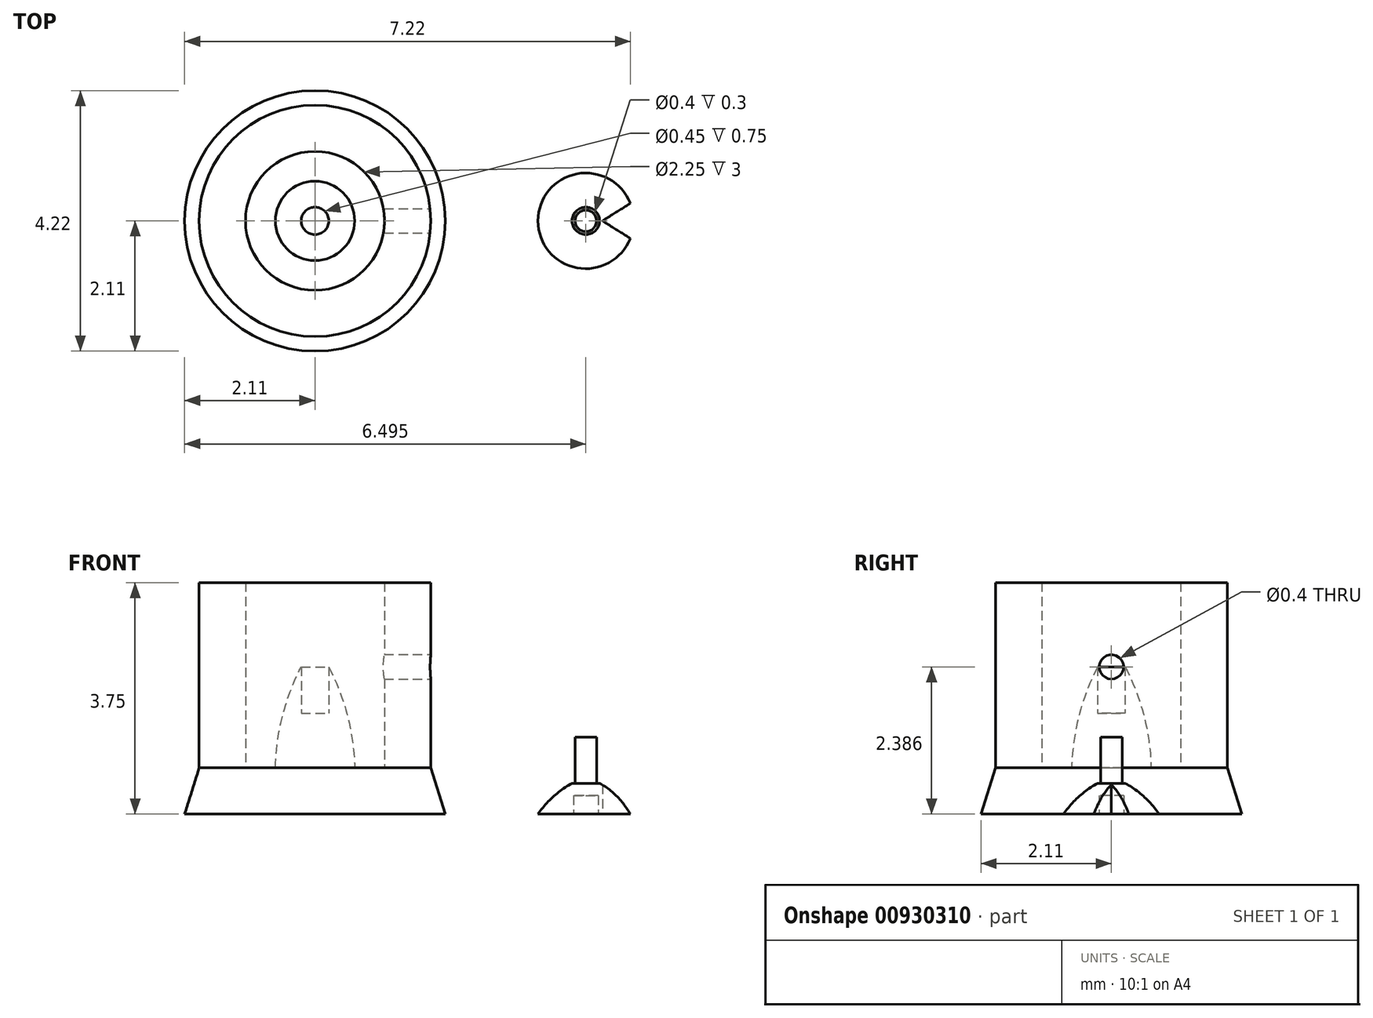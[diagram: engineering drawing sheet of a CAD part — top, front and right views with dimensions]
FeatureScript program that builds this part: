
annotation { "Feature Type Name" : "Feature", "Feature Type Description" : "" }
export const myFeature = defineFeature(function(context is Context, id is Id, definition is map)
    precondition{}
    {
        {
            var Q0;
            Q0=qCreatedBy(makeId("Front.planeOp"),FACE);
            var sketch = newSketch(context, id + "F0", { "sketchPlane" : qUnion([Q0])});
            skLineSegment(sketch, "E0", {"start": v(0, 0) * mm, "end": v(0, 0.89) * mm});
            skLineSegment(sketch, "E1", {"start": v(0.64, 0) * mm, "end": v(0.78, 0) * mm});
            skArc(sketch, "E2", {"start": v(0.78, 0) * mm, "mid": v(0.78, 0.1) * mm, "end": v(0.78, 0.2) * mm});
            skLineSegment(sketch, "E3", {"start": v(0.78, 0) * mm, "end": v(0.78, 25.4) * mm});
            skLineSegment(sketch, "E4", {"start": v(0.22, 1.55) * mm, "end": v(0.22, 1.64) * mm});
            skLineSegment(sketch, "E5", {"start": v(0.22, 1.64) * mm, "end": v(0.22, 0.89) * mm});
            skLineSegment(sketch, "E6", {"start": v(0.22, 0.89) * mm, "end": v(0, 0.89) * mm});
            skLineSegment(sketch, "E7", {"start": v(0.78, 0) * mm, "end": v(1.13, 0) * mm});
            skLineSegment(sketch, "E8", {"start": v(1.13, 0) * mm, "end": v(1.13, 3) * mm});
            skLineSegment(sketch, "E9", {"start": v(1.13, 3) * mm, "end": v(1.88, 3) * mm});
            skLineSegment(sketch, "E10", {"start": v(1.88, 3) * mm, "end": v(1.88, 0) * mm});
            skArc(sketch, "E11", {"start": v(0.64, 0) * mm, "mid": v(0.53, 0.84) * mm, "end": v(0.22, 1.64) * mm});
            skLineSegment(sketch, "E12", {"start": v(0, 0.94) * mm, "end": v(0.17, 0.94) * mm});
            skLineSegment(sketch, "E13", {"start": v(0.17, 0.95) * mm, "end": v(0.17, 0.94) * mm});
            skLineSegment(sketch, "E14", {"start": v(0.17, 0.94) * mm, "end": v(0.17, 1.68) * mm});
            skLineSegment(sketch, "E15", {"start": v(0.22, 1.69) * mm, "end": v(0.17, 1.69) * mm});
            skLineSegment(sketch, "E16", {"start": v(0.17, 1.65) * mm, "end": v(0.17, 1.69) * mm});
            skLineSegment(sketch, "E17", {"start": v(0.22, 2.19) * mm, "end": v(0.78, 2.19) * mm});
            skLineSegment(sketch, "E18", {"start": v(0.22, 2.19) * mm, "end": v(0, 2.19) * mm});
            skLineSegment(sketch, "E19.trimOffspring", {"start": v(0, 0.94) * mm, "end": v(0, 1.87) * mm});
            skLineSegment(sketch, "E20.trimOffspring", {"start": v(0, 0.94) * mm, "end": v(0, 25.4) * mm});
            skArc(sketch, "E21", {"start": v(0.22, 1.69) * mm, "mid": v(0.53, 1.9) * mm, "end": v(0.78, 2.19) * mm});
            skLineSegment(sketch, "E22", {"start": v(0, 0) * mm, "end": v(0, -0.75) * mm});
            skLineSegment(sketch, "E23", {"start": v(0, -0.75) * mm, "end": v(2.11, -0.75) * mm});
            skLineSegment(sketch, "E24", {"start": v(1.88, 0) * mm, "end": v(2.11, -0.75) * mm});
            skLineSegment(sketch, "E25", {"start": v(2.11, -0.75) * mm, "end": v(3.61, -0.75) * mm});
            skLineSegment(sketch, "E26", {"start": v(0.77, 2.19) * mm, "end": v(3.61, -0.75) * mm});
            skLineSegment(sketch, "E27", {"start": v(3.61, -0.75) * mm, "end": v(3.61, -1.83) * mm});
            skLineSegment(sketch, "E28", {"start": v(1.88, 1.64) * mm, "end": v(1.88, 1.96) * mm});
            skLineSegment(sketch, "E29", {"start": v(1.88, 1.96) * mm, "end": v(2.12, 1.64) * mm});
            skLineSegment(sketch, "E30", {"start": v(2.12, 1.64) * mm, "end": v(1.88, 1.64) * mm});
            skSolve(sketch);
        }
        {
            var Q0;
            Q0=makeQuery(id+"F0.imprint","IMPRINT",FACE,{"disambiguationData":[TD([[makeQuery(id+"F0.imprint","IMPRINT",EDGE,{"derivedFrom":sQuery(id+"F0.wireOp",EDGE,"E0")}),-1.0]])]});
            var Q1;
            {var subQ0=sQuery(id+"F0.wireOp",EDGE,"E9");Q1=makeQuery(id+"F0.imprint","IMPRINT",FACE,{"disambiguationData":[TD([[makeQuery(id+"F0.imprint","IMPRINT",EDGE,{"derivedFrom":subQ0}),-1.0]])]});}
            var Q2;
            Q2=sQuery(id+"F0.wireOp",EDGE,"E20.trimOffspring");
            revolve(context, id + "F1", {"surfaceOperationType" : NewSurfaceOperationType.NEW, "entities" : qUnion([Q0, Q1]), "axis" : qUnion([Q2]), "revolveType" : RevolveType.FULL});
        }
        {
            var Q0;
            {var subQ3=sQuery(id+"F0.wireOp",EDGE,"E12");Q0=makeQuery(id+"F0.imprint","IMPRINT",FACE,{"disambiguationData":[TD([[makeQuery(id+"F0.imprint","IMPRINT",EDGE,{"derivedFrom":subQ3}),1.0]])]});}
            var Q1;
            Q1=sQuery(id+"F0.wireOp",EDGE,"E20.trimOffspring");
            revolve(context, id + "F2", {"surfaceOperationType" : NewSurfaceOperationType.NEW, "entities" : qUnion([Q0]), "axis" : qUnion([Q1]), "revolveType" : RevolveType.FULL});
        }
        {
            var Q0;
            Q0=makeQuery(id+"F2.opRevolve","SWEPT_BODY",BODY,{"disambiguationData":[OSD([sQuery(id+"F0.wireOp",EDGE,"E12"),sQuery(id+"F0.wireOp",EDGE,"E14"),sQuery(id+"F0.wireOp",EDGE,"E15"),sQuery(id+"F0.wireOp",EDGE,"E16"),sQuery(id+"F0.wireOp",EDGE,"E17"),sQuery(id+"F0.wireOp",EDGE,"E18"),sQuery(id+"F0.wireOp",EDGE,"E20.trimOffspring"),sQuery(id+"F0.wireOp",EDGE,"E21")])]});
            var Q1;
            Q1=sQuery(id+"F0.wireOp",EDGE,"E26");
            transform(context, id + "F3", {"entities" : qUnion([Q0]), "transformType" : TransformType.TRANSLATION_ENTITY, "oppositeDirectionEntity" : false, "transformLine" : qUnion([Q1]), "makeCopy" : false});
        }
        {
            var Q0;
            Q0=makeQuery(id+"F2.opRevolve","SWEPT_BODY",BODY,{"disambiguationData":[OSD([sQuery(id+"F0.wireOp",EDGE,"E12"),sQuery(id+"F0.wireOp",EDGE,"E14"),sQuery(id+"F0.wireOp",EDGE,"E15"),sQuery(id+"F0.wireOp",EDGE,"E16"),sQuery(id+"F0.wireOp",EDGE,"E17"),sQuery(id+"F0.wireOp",EDGE,"E18"),sQuery(id+"F0.wireOp",EDGE,"E20.trimOffspring"),sQuery(id+"F0.wireOp",EDGE,"E21")])]});
            var Q1;
            Q1=sQuery(id+"F0.wireOp",EDGE,"E27");
            transform(context, id + "F4", {"entities" : qUnion([Q0]), "transformType" : TransformType.ROTATION, "transformAxis" : qUnion([Q1]), "angle" : 180 * degree, "makeCopy" : false});
        }
        {
            var Q0;
            Q0=makeQuery(id+"F2.opRevolve","SWEPT_BODY",BODY,{"disambiguationData":[OSD([sQuery(id+"F0.wireOp",EDGE,"E12"),sQuery(id+"F0.wireOp",EDGE,"E14"),sQuery(id+"F0.wireOp",EDGE,"E15"),sQuery(id+"F0.wireOp",EDGE,"E16"),sQuery(id+"F0.wireOp",EDGE,"E17"),sQuery(id+"F0.wireOp",EDGE,"E18"),sQuery(id+"F0.wireOp",EDGE,"E20.trimOffspring"),sQuery(id+"F0.wireOp",EDGE,"E21")])]});
            var Q1;
            Q1=sQuery(id+"F0.wireOp",EDGE,"E25");
            transform(context, id + "F5", {"entities" : qUnion([Q0]), "transformType" : TransformType.ROTATION, "transformAxis" : qUnion([Q1]), "angle" : 180 * degree, "makeCopy" : false});
        }
        {
            var Q0;
            Q0=makeQuery(id+"F2.opRevolve","SWEPT_FACE",FACE,{"disambiguationData":[OSD([sQuery(id+"F0.wireOp",EDGE,"E17"),sQuery(id+"F0.wireOp",EDGE,"E18")])]});
            var sketch = newSketch(context, id + "F6", { "sketchPlane" : qUnion([Q0])});
            skLineSegment(sketch, "E31", {"start": v(4.39, 0) * mm, "end": v(5.16, 0) * mm});
            skCircle(sketch, "E32", {"center": v(4.39, 0) * mm, "radius": 0.2 * mm});
            skLineSegment(sketch, "E33", {"start": v(5.1, 0.28) * mm, "end": v(4.65, 0) * mm});
            skLineSegment(sketch, "E34", {"start": v(4.65, 0) * mm, "end": v(5.1, -0.28) * mm});
            skPoint(sketch, "E35.start.orphan", {"position": v(4.77, 0) * mm});
            skSolve(sketch);
        }
        {
            var Q0;
            Q0=makeQuery(id+"F6.imprint","IMPRINT",FACE,{"disambiguationData":[TD([[makeQuery(id+"F6.imprint","IMPRINT",EDGE,{"derivedFrom":sQuery(id+"F6.wireOp",EDGE,"E32")}),1.0]])]});
            extrude(context, id + "F7", {"entities" : qUnion([Q0]), "operationType" : NewBodyOperationType.REMOVE, "oppositeDirection" : true, "depth" : .3 * mm, "offsetDistance" : 25.4 * mm});
        }
        {
            var Q0;
            {var subQ3=sQuery(id+"F6.wireOp",EDGE,"E33");Q0=makeQuery(id+"F6.imprint","IMPRINT",FACE,{"disambiguationData":[TD([[makeQuery(id+"F6.imprint","IMPRINT",EDGE,{"derivedFrom":subQ3}),1.0]])]});}
            var Q1;
            {var subQ3=sQuery(id+"F6.wireOp",EDGE,"E34");Q1=makeQuery(id+"F6.imprint","IMPRINT",FACE,{"disambiguationData":[TD([[makeQuery(id+"F6.imprint","IMPRINT",EDGE,{"derivedFrom":subQ3}),1.0]])]});}
            extrude(context, id + "F8", {"entities" : qUnion([Q0, Q1]), "operationType" : NewBodyOperationType.REMOVE, "endBound" : BoundingType.THROUGH_ALL, "oppositeDirection" : true, "depth" : 25.4 * mm, "offsetDistance" : 25.4 * mm});
        }
        {
            var Q0;
            Q0=sQuery(id+"F0.wireOp",VERTEX,"E28.start");
            var Q1;
            Q1=qCreatedBy(makeId("Right.planeOp"),FACE);
            cPlane(context, id + "F9", {"entities" : qUnion([Q0, Q1]), "cplaneType" : CPlaneType.PLANE_POINT, "offset" : 25.4 * mm, "width" : 152.4 * mm, "height" : 152.4 * mm});
        }
        {
            var Q0;
            Q0=qCreatedBy(id+"F9.planeOp",FACE);
            var sketch = newSketch(context, id + "F10", { "sketchPlane" : qUnion([Q0])});
            skCircle(sketch, "E36", {"center": v(0, 1.64) * mm, "radius": 0.2 * mm});
            skSolve(sketch);
        }
        {
            var Q0;
            Q0=makeQuery(id+"F10.imprint","IMPRINT",FACE,{"disambiguationData":[TD([[makeQuery(id+"F10.imprint","IMPRINT",EDGE,{"derivedFrom":sQuery(id+"F10.wireOp",EDGE,"E36")}),1.0]])]});
            var Q1;
            Q1=makeQuery(id+"F1.opRevolve","SWEPT_FACE",FACE,{"disambiguationData":[OSD([sQuery(id+"F0.wireOp",EDGE,"E8")])]});
            extrude(context, id + "F11", {"entities" : qUnion([Q0]), "operationType" : NewBodyOperationType.REMOVE, "endBound" : BoundingType.UP_TO_SURFACE, "oppositeDirection" : true, "depth" : 25.4 * mm, "endBoundEntityFace" : qUnion([Q1]), "offsetDistance" : 25.4 * mm});
        }
    });
